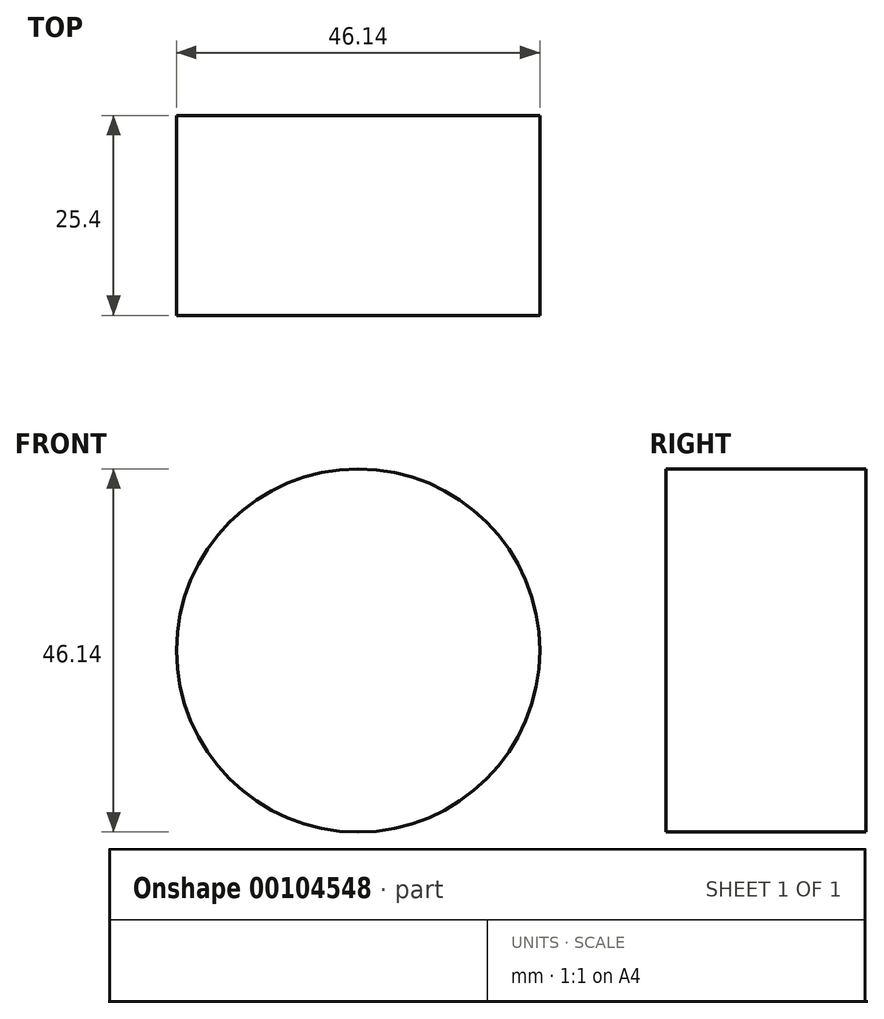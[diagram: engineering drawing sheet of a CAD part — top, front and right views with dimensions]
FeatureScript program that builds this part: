
annotation { "Feature Type Name" : "Feature", "Feature Type Description" : "" }
export const myFeature = defineFeature(function(context is Context, id is Id, definition is map)
    precondition{}
    {
        {
            var Q0;
            Q0=qCreatedBy(makeId("Front.planeOp"),FACE);
            var sketch = newSketch(context, id + "F0", { "sketchPlane" : qUnion([Q0])});
            skCircle(sketch, "E0", {"center": v(0, 0) * mm, "radius": 23.07 * mm});
            skSolve(sketch);
        }
        {
            var Q0;
            Q0=makeQuery(id+"F0.imprint","IMPRINT",FACE,{"disambiguationData":[TD([[makeQuery(id+"F0.imprint","IMPRINT",EDGE,{"derivedFrom":sQuery(id+"F0.wireOp",EDGE,"E0")}),1.0]])]});
            extrude(context, id + "F1", {"entities" : qUnion([Q0]), "depth" : 25.4 * mm});
        }
    });
